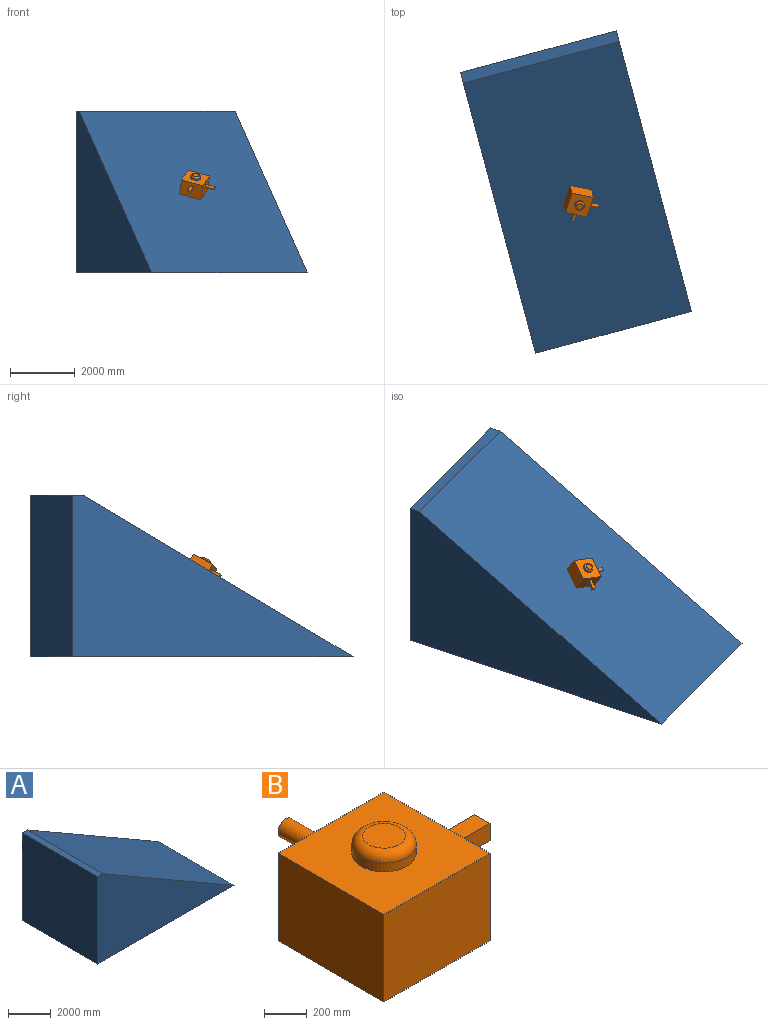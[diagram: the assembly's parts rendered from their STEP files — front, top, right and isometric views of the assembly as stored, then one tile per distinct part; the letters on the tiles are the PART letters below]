
ASSEMBLY  parts=2 mates=1
PART A: 6 faces, bbox 9000x5000x5000 mm
  f0: plane 9000x5000mm, normal (0,-1,0), area 23349364.9mm2, adj f1,f2,f4,f5
  f1: plane 5000x339.75mm, normal (0,0,1), area 1698729.8mm2, adj f0,f3,f4,f5
  f2: plane 9000x5000mm, normal (0,0,-1), area 45000000mm2, adj f0,f3,f4,f5
  f3: plane 9000x5000mm, normal (0,1,0), area 23349364.9mm2, adj f1,f2,f4,f5
  f4: plane 8660.25x5000mm, normal (0.5,0,0.87), area 50000000mm2, adj f0,f1,f2,f3
  f5: plane 5000x5000mm, normal (-1,0,0), area 25000000mm2, adj f0,f1,f2,f3
PART B: 16 faces, bbox 1000x1000x600 mm
  f0: plane 700x500mm, normal (-1,0,0), area 350000mm2, adj f1,f3,f4,f5
  f1: plane 700x500mm, normal (0,-1,0), area 350000mm2, adj f0,f2,f4,f5
  f2: plane 700x500mm, normal (1,0,0), area 340000mm2, adj f1,f3,f4,f5,f9,f10,f11,f12
  f3: plane 700x500mm, normal (0,1,0), area 342146mm2, adj f0,f2,f4,f5,f14
  f4: plane 700x700mm, normal (0,0,1), area 419314.2mm2, adj f0,f1,f2,f3,f6
  f5: plane 700x700mm, normal (0,0,-1), area 490000mm2, adj f0,f1,f2,f3
  f6: cylinder r=150mm len=300mm, axis (0,0,-1), area 47123.9mm2, adj f4,f8
  f7: plane 200x200mm, normal (0,0,1), area 31415.9mm2, adj f8
  f8: torus R=100mm, axis (0,0,1), area 65056mm2, adj f6,f7
  f9: plane 300x100mm, normal (0,0,1), area 30000mm2, adj f2,f10,f12,f13
  f10: plane 300x100mm, normal (0,-1,0), area 30000mm2, adj f2,f9,f11,f13
  f11: plane 300x100mm, normal (0,0,-1), area 30000mm2, adj f2,f10,f12,f13
  f12: plane 300x100mm, normal (0,1,0), area 30000mm2, adj f2,f9,f11,f13
  f13: plane 100x100mm, normal (1,0,0), area 10000mm2, adj f9,f10,f11,f12
  f14: cylinder r=50mm len=300mm, axis (0,-1,0), area 94247.8mm2, adj f3,f15
  f15: plane 100x100mm, normal (0,1,0), area 7854mm2, adj f14
PLACE A rot(axis=(0,0,-1),75deg) t=(321.42,4518.18,18510.93)mm fixed
PLACE B rot(axis=(0.12,0.3,-0.95),108deg) t=(768.46,2951.22,21002.95)mm
MATE revolute B.f6 <-> A.f4  axis (-0.13,0.48,-0.87) through (763.67,2964.26,21010.93)mm
